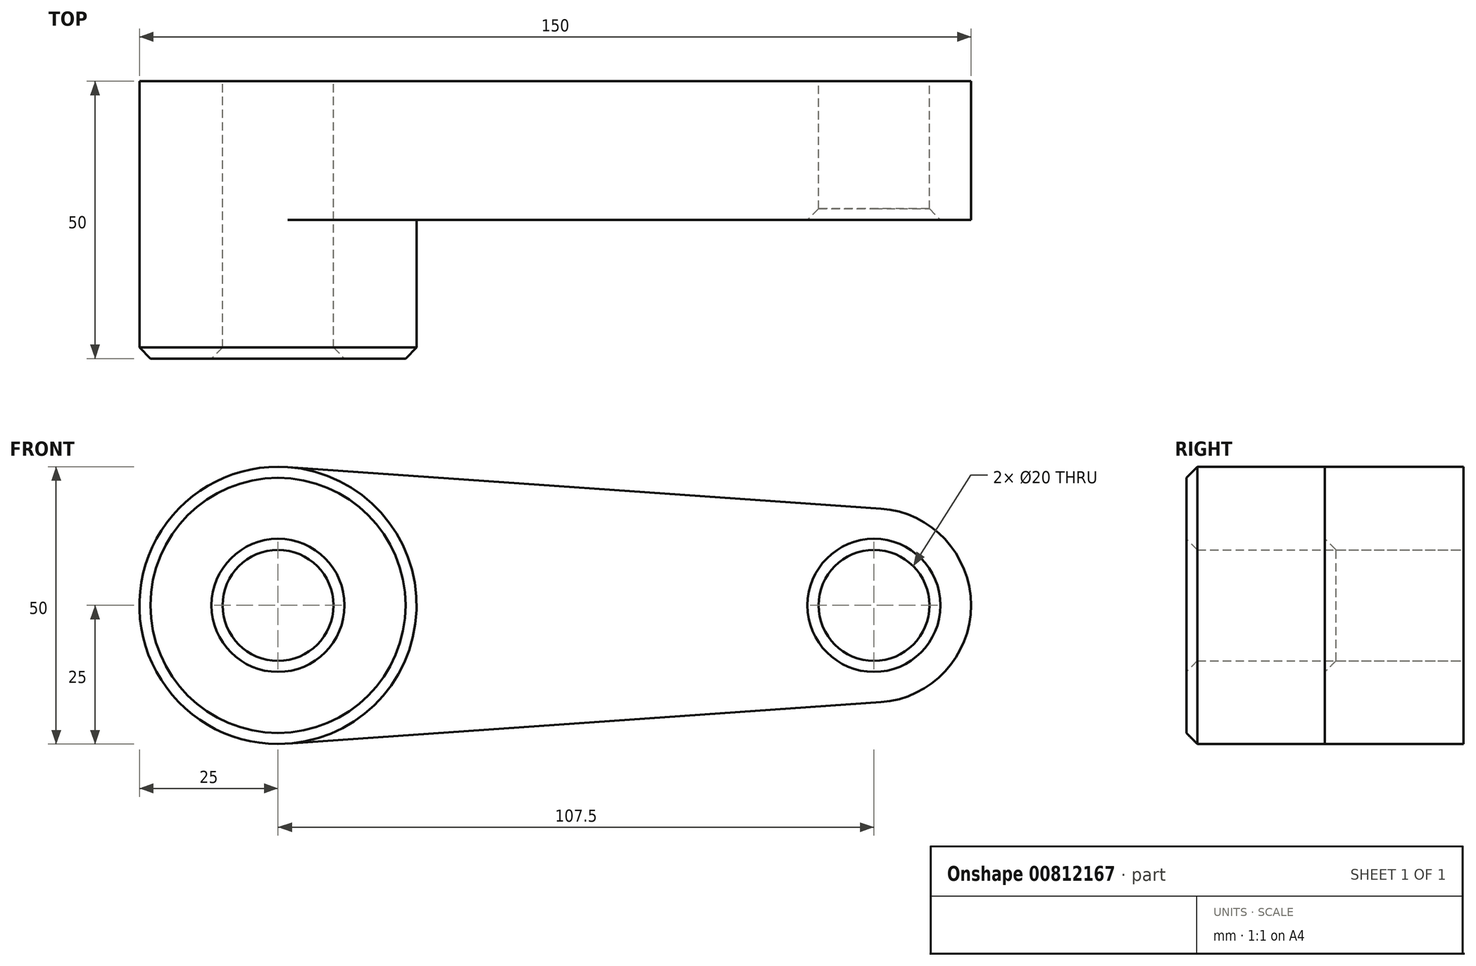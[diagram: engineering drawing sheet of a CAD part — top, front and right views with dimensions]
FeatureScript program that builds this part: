
annotation { "Feature Type Name" : "Feature", "Feature Type Description" : "" }
export const myFeature = defineFeature(function(context is Context, id is Id, definition is map)
    precondition{}
    {
        {
            var Q0;
            Q0=qCreatedBy(makeId("Front.planeOp"),FACE);
            var sketch = newSketch(context, id + "F0", { "sketchPlane" : qUnion([Q0])});
            skCircle(sketch, "E0", {"center": v(0, 0) * mm, "radius": 25 * mm});
            skCircle(sketch, "E1", {"center": v(107.5, 0) * mm, "radius": 17.5 * mm});
            skLineSegment(sketch, "E2", {"start": v(1.74, 24.94) * mm, "end": v(108.72, 17.46) * mm});
            skLineSegment(sketch, "E3", {"start": v(1.74, -24.94) * mm, "end": v(108.72, -17.46) * mm});
            skCircle(sketch, "E4", {"center": v(0, 0) * mm, "radius": 10 * mm});
            skCircle(sketch, "E5", {"center": v(107.5, 0) * mm, "radius": 10 * mm});
            skSolve(sketch);
        }
        {
            var Q0;
            {var subQ0=sQuery(id+"F0.wireOp",EDGE,"E2");Q0=makeQuery(id+"F0.imprint","IMPRINT",FACE,{"disambiguationData":[TD([[makeQuery(id+"F0.imprint","IMPRINT",EDGE,{"derivedFrom":subQ0}),-1.0]])]});}
            var Q1;
            Q1 = qSketchRegion(id + "F0", true);
            extrude(context, id + "F1", {"entities" : qUnion([Q0, Q1]), "depth" : 25 * mm, "offsetDistance" : 25 * mm});
        }
        {
            var Q0;
            Q0=makeQuery(id+"F0.imprint","IMPRINT",FACE,{"disambiguationData":[TD([[makeQuery(id+"F0.imprint","IMPRINT",EDGE,{"derivedFrom":sQuery(id+"F0.wireOp",EDGE,"E4")}),-1.0]])]});
            extrude(context, id + "F2", {"entities" : qUnion([Q0]), "operationType" : NewBodyOperationType.ADD, "depth" : 50 * mm, "offsetDistance" : 25 * mm});
        }
        {
            var Q0;
            Q0=makeQuery(id+"F2.opExtrude","CAP_EDGE",EDGE,{"disambiguationData":[OSD([sQuery(id+"F0.wireOp",EDGE,"E4")])],"isStart":false});
            var Q1;
            Q1=makeQuery(id+"F2.opExtrude","CAP_FACE",FACE,{"disambiguationData":[OSD([sQuery(id+"F0.wireOp",EDGE,"E0"),sQuery(id+"F0.wireOp",EDGE,"E4")])],"isStart":false});
            var Q2;
            Q2=makeQuery(id+"F1.opExtrude","CAP_EDGE",EDGE,{"disambiguationData":[OSD([sQuery(id+"F0.wireOp",EDGE,"E5")])],"isStart":false});
            chamfer(context, id + "F3", {"entities" : qUnion([Q0, Q1, Q2]), "width" : 2 * mm, "tangentPropagation" : true});
        }
    });
